# Revit family: Gleitlager T HV2, m.D., Ø64 bis Ø219mm (h=126-152mm)
name_source: partatom
category: HLS-Bauteile
units: mm (PartAtom-declared; Revit-internal decimal feet)

## family parameters
Arbeitsebenenbasiert = Ja
Beim Laden mit Abzugskörper schneiden = Nein
Bemaßung runder Anschluss = Durchmesser verwenden
Beschriftungsausrichtung beibehalten = Nein
Gemeinsam genutzt = Ja
Immer vertikal = Nein
Klassifizierung = Keine
Raumberechnungspunkt = Nein
Teiletyp = Normal

## types (13) — shared parameters
Anzahl Rohrschellen = 2
Baustoffklasse = B2
Breite Schellenband = 50 mm
Breite Unterbau = 100 mm
Dämmstärke = 6 mm  [stored 0.019685 ft]
Fabrikat = MEFA
Hersteller = MEFA
Kurztext1 = Gleitlager T 2 RS HV2 50x5
Länge Unterbau = 250 mm
Material = Stahl
Materialname = S235
Mengeneinheit = St
Schalldämmeinlage = Gummi EPDM
Sicherheitsfaktor = 1.54
Stärke Material = 8 mm  [stored 0.0262467 ft]
Stärke Schellenband = 5 mm
Verschluss = Mutter / Verschluss-Schraube
Vorgabe-Ansicht = 1219 mm
max. Höhe Unterbau = 150 mm
max. Temperaturbeständigkeit = 100 °C
min. Höhe Unterbau = 125 mm
vpe = 1
zero-valued in all types: max. Rohraußendurchmesser, min. Rohraußendurchmesser

## per-type parameters (varying)
| type | Artikelnummer | EAN | Gewicht | Gewicht pro Bauteil | Kurztext2 | Nennweite DN Rohr | Rohraußendurchmesser | Schellenteil | max. Rohrachse | min. Rohrachse |
| Gleitlager T HV2, m.2 RS, m.D., Ø 64 (h=126-152mm) | 141bfbb0064 | 4250928461223 | 5.35 kg | 5.35 kg | 64 mm EPDM 100x250 mm fsv | 0 mm  [stored 0 ft] | 64 mm  [stored 0.209974 ft] | TL-141S_b0076 bis 0231, m.D : mit RS Ø64mm m.D | 184 mm | 158 mm |
| Gleitlager T HV2, m.2 RS, m.D., Ø 76 (h=126-152mm) | 141bfbb0076 | 4250928461230 | 5.56 kg | 5.56 kg | 76 mm EPDM 100x250 mm fsv | 65 mm  [stored 0.213255 ft] | 76 mm  [stored 0.249344 ft] | TL-141S_b0076 bis 0231, m.D : mit RS Ø76mm m.D | 190 mm | 164 mm |
| Gleitlager T HV2, m.2 RS, m.D., Ø 89 (h=126-152mm) | 141bfbb0089 | 4250928461247 | 5.76 kg | 5.76 kg | 89 mm EPDM 100x250 mm fsv | 80 mm  [stored 0.262467 ft] | 89 mm  [stored 0.291995 ft] | TL-141S_b0076 bis 0231, m.D : mit RS Ø88.9mm, m.D | 197 mm | 171 mm |
| Gleitlager T HV2, m.2 RS, m.D., Ø108 (h=126-152mm) | 141bfbb0108 | 4250928461254 | 6.06 kg | 6.06 kg | 108 mm EPDM 100x250 mm fsv | 0 mm  [stored 0 ft] | 108 mm  [stored 0.354331 ft] | TL-141S_b0076 bis 0231, m.D : mit RS Ø108mm m.D | 206 mm | 180 mm |
| Gleitlager T HV2, m.2 RS, m.D., Ø110 (h=126-152mm) | 141bfbb0110 | 4250928461261 | 6.10 kg | 6.10 kg | 110 mm EPDM 100x250 mm fsv | 0 mm  [stored 0 ft] | 110 mm  [stored 0.360892 ft] | TL-141S_b0076 bis 0231, m.D : mit RS Ø110mm m.D | 207 mm | 181 mm |
| Gleitlager T HV2, m.2 RS, m.D., Ø114 (h=126-152mm) | 141bfbb0114 | 4250928461278 | 6.16 kg | 6.16 kg | 114 mm EPDM 100x250 mm fsv | 100 mm  [stored 0.328084 ft] | 114 mm  [stored 0.374016 ft] | TL-141S_b0076 bis 0231, m.D : mit RS Ø114.3mm m.D | 209 mm | 183 mm |
| Gleitlager T HV2, m.2 RS, m.D., Ø133 (h=126-152mm) | 141bfbb0133 | 4250928461285 | 6.46 kg | 6.46 kg | 133 mm EPDM 100x250 mm fsv | 0 mm  [stored 0 ft] | 133 mm  [stored 0.436352 ft] | TL-141S_b0076 bis 0231, m.D : mit RS Ø133mm m.D | 219 mm | 193 mm |
| Gleitlager T HV2, m.2 RS, m.D., Ø140 (h=126-152mm) | 141bfbb0140 | 4250928461292 | 6.58 kg | 6.58 kg | 140 mm EPDM 100x250 mm fsv | 125 mm  [stored 0.410105 ft] | 140 mm  [stored 0.459318 ft] | TL-141S_b0076 bis 0231, m.D : mit RS Ø139.7mm m.D | 222 mm | 196 mm |
| Gleitlager T HV2, m.2 RS, m.D., Ø160 (h=126-152mm) | 141bfbb0160 | 4250928461308 | 6.90 kg | 6.90 kg | 160 mm EPDM 100x250 mm fsv | 0 mm  [stored 0 ft] | 160 mm  [stored 0.524934 ft] | TL-141S_b0076 bis 0231, m.D : mit RS Ø160mm m.D | 232 mm | 206 mm |
| Gleitlager T HV2, m.2 RS, m.D., Ø168 (h=126-152mm) | 141bfbb0168 | 4250928461315 | 7.03 kg | 7.03 kg | 168 mm EPDM 100x250 mm fsv | 150 mm  [stored 0.492126 ft] | 168 mm  [stored 0.551181 ft] | TL-141S_b0076 bis 0231, m.D : mit RS Ø168.3mm m.D | 236 mm | 210 mm |
| Gleitlager T HV2, m.2 RS, m.D., Ø180 (h=126-152mm) | 141bfbb0180 | 4250928461322 | 7.22 kg | 7.22 kg | 180 mm EPDM 100x250 mm fsv | 0 mm  [stored 0 ft] | 180 mm  [stored 0.590551 ft] | TL-141S_b0076 bis 0231, m.D : mit RS Ø180mm m.D | 242 mm | 216 mm |
| Gleitlager T HV2, m.2 RS, m.D., Ø210 (h=126-152mm) | 141bfbb0210 | 4250928461339 | 7.70 kg | 7.70 kg | 210 mm EPDM 100x250 mm fsv | 0 mm  [stored 0 ft] | 210 mm  [stored 0.688976 ft] | TL-141S_b0076 bis 0231, m.D : mit RS Ø210mm m.D | 257 mm | 231 mm |
| Gleitlager T HV2, m.2 RS, m.D., Ø219 (h=126-152mm) | 141bfbb0219 | 4250928461346 | 7.84 kg | 7.84 kg | 219 mm EPDM 100x250 mm fsv | 200 mm  [stored 0.656168 ft] | 219 mm  [stored 0.718504 ft] | TL-141S_b0076 bis 0231, m.D : mit RS Ø219mm m.D | 262 mm | 236 mm |

note: [stored X ft] marks values corroborated as IEEE doubles in the binary element streams (Revit-internal decimal feet)

## geometry (parser evidence)
native form markers: Sweep x9
no freeform markers — native parametric forms only
